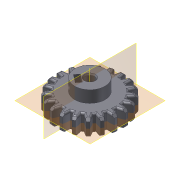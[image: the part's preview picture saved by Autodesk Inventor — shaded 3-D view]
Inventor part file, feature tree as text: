
AUTODESK INVENTOR PART (.ipt)
format: ipt  version: 2015 SP2 (Build 190223200, 223)  size: 939,520 bytes
history: native  units: mm (DEFAULTED — no unit token found)
features: plane x6, sketch x6, extrude x4, other x3, chamfer x2, fillet x2, hole x1, revolve x1, mirror x1
ambient origin geometry x8: Origin, YZ Plane, XZ Plane, XY Plane, X Axis, Y Axis, Z Axis, Center Point
bodies: Body1 (feature_tree), Body2 (feature_tree)
feature tree (26):
  extrude  "Extrusion1"  Depth=10.0mm TaperAngle=0.0deg
  plane  "Work Plane2"
  plane  "Work Plane8"
  plane  "Work Plane9"
  other  "Engranaje recto"
  extrude  "Extrusión2"  Depth=10.0mm TaperAngle=0.0deg
  hole  "Agujero1"  [1 undecoded]
  plane  "Plano de trabajo12"
  extrude  "Extrusión3"  TaperAngle=0.0deg  [1 undecoded]
  extrude  "Extrusión4"  Depth=37.0mm
  chamfer  "Chaflán1"  [1 undecoded]
  chamfer  "Chaflán2"  Distance=7.0mm
  revolve  "Revolución2"  [1 undecoded]
  plane  "Plano de trabajo13"
  mirror  "Simetría1"
  fillet  "Empalme1"  Radius=6.0mm
  fillet  "Empalme2"  Radius=7.0mm
  sketch  "Sketch1"  dims[d0=40.75mm d1=10.0mm d2=0.0mm]
  sketch  "Sketch2"  dims[d3=37.0mm d4=10.0mm d5=0.0mm]
  other  "Srf1"
  sketch  "Boceto3"  dims[d16=37.0mm d17=0.0mm d34=1.495997mm]
  plane  "Plano de trabajo11"
  sketch  "Boceto4"  dims[d39=0.0mm d41=0.0mm]
  sketch  "Boceto5"  dims[d43=37.0mm d46=37.0mm d47=0.0mm d48=0.0mm]
  sketch  "Boceto6"  dims[d49=18.0mm d50=7.0mm d51=0.0mm d86=10.0mm d87=10.0mm d54=5.6mm d55=6.0mm d56=4.0mm d57=2.0mm d58=90.0deg d59=8.0mm d60=20.594885mm d61=-2.4mm d62=6.0mm d63=7.0mm d64=4.0mm d65=3.0mm d66=0.0mm d67=3.6mm d68=2.8mm d69=0.0mm d70=0.5mm d71=2.0mm d72=60.0deg d73=1.0mm d74=2.0mm d75=60.0deg d76=0.5mm d77=0.5mm d78=2.0mm d79=2.0mm d81=90.0deg d82=1.0mm d83=1.0mm]
  other  "Diámetro de separación"
note: 4 required parameter values undecoded (feature->parameter linkage not recoverable at this tier; creation-order binding heuristic only, values carry confidence <= 0.55)